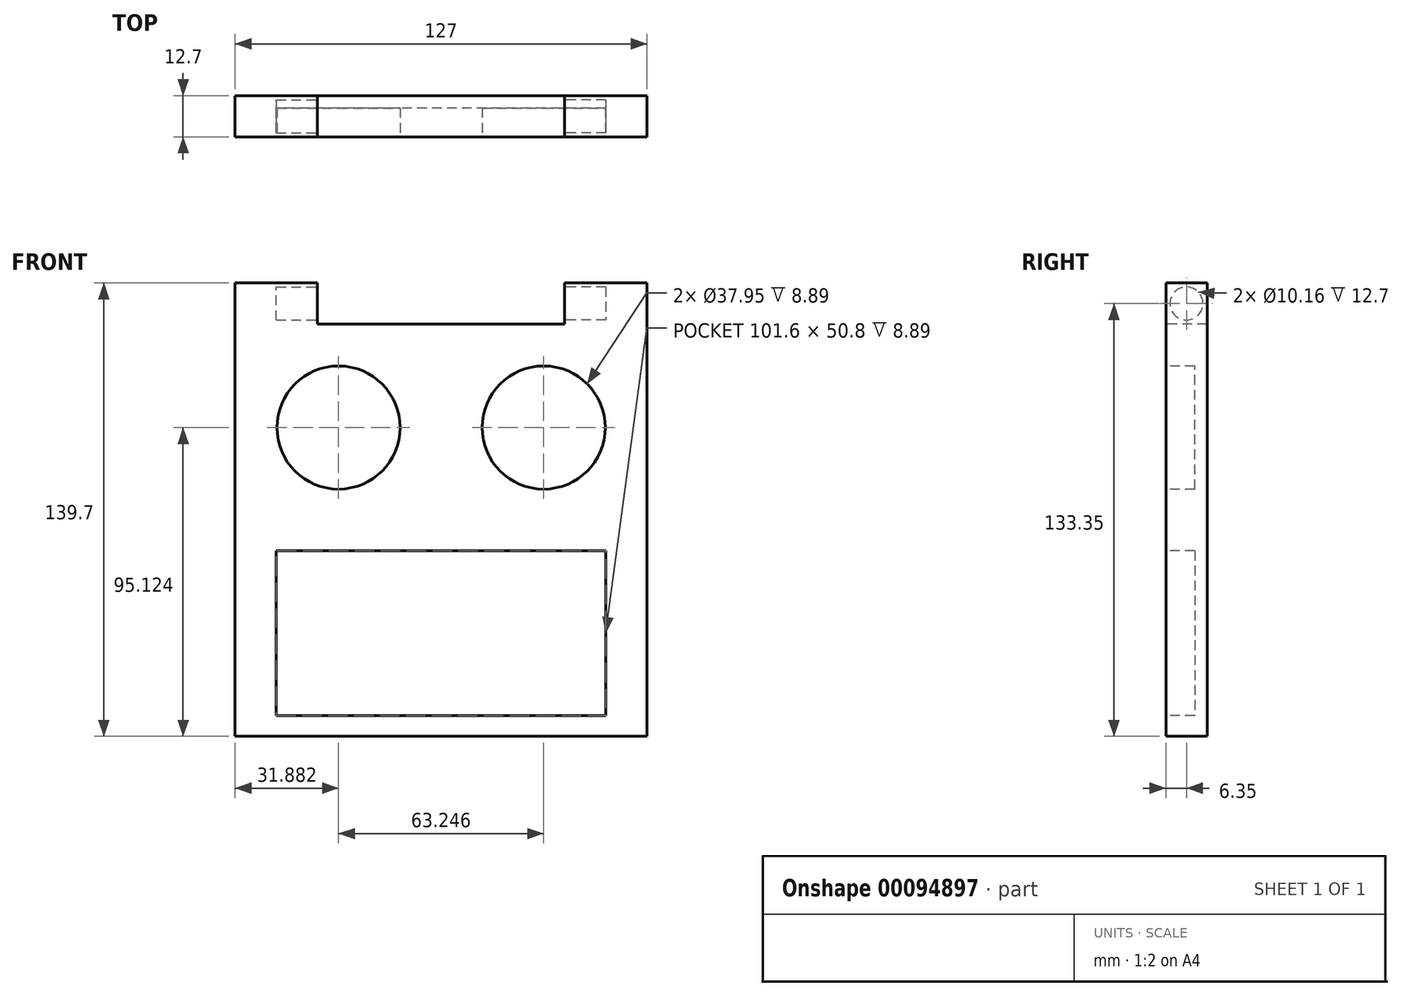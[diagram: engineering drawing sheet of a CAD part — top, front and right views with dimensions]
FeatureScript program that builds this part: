
annotation { "Feature Type Name" : "Feature", "Feature Type Description" : "" }
export const myFeature = defineFeature(function(context is Context, id is Id, definition is map)
    precondition{}
    {
        {
            var Q0;
            Q0=qCreatedBy(makeId("Front.planeOp"),FACE);
            var sketch = newSketch(context, id + "F0", { "sketchPlane" : qUnion([Q0])});
            skLineSegment(sketch, "E0", {"start": v(0, 0) * mm, "end": v(0, 127) * mm});
            skLineSegment(sketch, "E1", {"start": v(0, 127) * mm, "end": v(127, 127) * mm});
            skLineSegment(sketch, "E2", {"start": v(127, 127) * mm, "end": v(127, 0) * mm});
            skLineSegment(sketch, "E3", {"start": v(127, 0) * mm, "end": v(0, 0) * mm});
            skSolve(sketch);
        }
        {
            var Q0;
            Q0=qSketchRegion(id+"F0",true);
            extrude(context, id + "F1", {"entities" : qUnion([Q0]), "depth" : 12.7 * mm});
        }
        {
            var Q0;
            Q0=makeQuery(id+"F1.opExtrude","CAP_FACE",FACE,{"disambiguationData":[OSD([sQuery(id+"F0.wireOp",EDGE,"E0"),sQuery(id+"F0.wireOp",EDGE,"E1"),sQuery(id+"F0.wireOp",EDGE,"E2"),sQuery(id+"F0.wireOp",EDGE,"E3")])],"isStart":false});
            var sketch = newSketch(context, id + "F2", { "sketchPlane" : qUnion([Q0])});
            skCircle(sketch, "E4", {"center": v(95.13, 95.12) * mm, "radius": 18.97 * mm});
            skCircle(sketch, "E5", {"center": v(31.88, 95.12) * mm, "radius": 18.97 * mm});
            skLineSegment(sketch, "E6", {"start": v(12.7, 57.15) * mm, "end": v(12.7, 6.35) * mm});
            skLineSegment(sketch, "E7", {"start": v(12.7, 6.35) * mm, "end": v(114.3, 6.35) * mm});
            skLineSegment(sketch, "E8", {"start": v(114.3, 6.35) * mm, "end": v(114.3, 57.15) * mm});
            skLineSegment(sketch, "E9", {"start": v(114.3, 57.15) * mm, "end": v(12.7, 57.15) * mm});
            skSolve(sketch);
        }
        {
            var Q0;
            Q0=qSketchRegion(id+"F2",true);
            extrude(context, id + "F3", {"entities" : qUnion([Q0]), "operationType" : NewBodyOperationType.REMOVE, "oppositeDirection" : true, "depth" : 8.9 * mm});
        }
        {
            var Q0;
            Q0=makeQuery(id+"F1.opExtrude","SWEPT_FACE",FACE,{"disambiguationData":[OSD([sQuery(id+"F0.wireOp",EDGE,"E1")])]});
            var sketch = newSketch(context, id + "F4", { "sketchPlane" : qUnion([Q0])});
            skLineSegment(sketch, "E10", {"start": v(0, 0) * mm, "end": v(25.4, 0) * mm});
            skLineSegment(sketch, "E11", {"start": v(25.4, 0) * mm, "end": v(25.4, -12.7) * mm});
            skLineSegment(sketch, "E12", {"start": v(25.4, -12.7) * mm, "end": v(0, -12.7) * mm});
            skLineSegment(sketch, "E13", {"start": v(0, -12.7) * mm, "end": v(0, 0) * mm});
            skSolve(sketch);
        }
        {
            var Q0;
            Q0 = qSketchRegion(id + "F4", true);
            extrude(context, id + "F5", {"entities" : qUnion([Q0]), "operationType" : NewBodyOperationType.ADD, "depth" : 12.7 * mm});
        }
        {
            var Q0;
            Q0=makeQuery(id+"F5.opExtrude","SWEPT_FACE",FACE,{"disambiguationData":[OSD([sQuery(id+"F4.wireOp",EDGE,"E11")])]});
            var sketch = newSketch(context, id + "F6", { "sketchPlane" : qUnion([Q0])});
            skCircle(sketch, "E14", {"center": v(-6.35, 133.35) * mm, "radius": 5.08 * mm});
            skPoint(sketch, "E15.trimOffspring.end.orphan", {"position": v(-6.35, 127) * mm});
            skPoint(sketch, "E16.start.orphan", {"position": v(-6.35, 139.7) * mm});
            skSolve(sketch);
        }
        {
            var Q0;
            Q0=makeQuery(id+"F1.opExtrude","SWEPT_FACE",FACE,{"disambiguationData":[OSD([sQuery(id+"F0.wireOp",EDGE,"E1")])]});
            var sketch = newSketch(context, id + "F7", { "sketchPlane" : qUnion([Q0])});
            skLineSegment(sketch, "E17", {"start": v(127, 0) * mm, "end": v(101.6, 0) * mm});
            skLineSegment(sketch, "E18", {"start": v(101.6, 0) * mm, "end": v(101.6, -12.7) * mm});
            skLineSegment(sketch, "E19", {"start": v(101.6, -12.7) * mm, "end": v(127, -12.7) * mm});
            skLineSegment(sketch, "E20", {"start": v(127, -12.7) * mm, "end": v(127, 0) * mm});
            skSolve(sketch);
        }
        {
            var Q0;
            Q0 = qSketchRegion(id + "F7", true);
            extrude(context, id + "F8", {"entities" : qUnion([Q0]), "operationType" : NewBodyOperationType.ADD, "depth" : 12.7 * mm});
        }
        {
            var Q0;
            Q0=makeQuery(id+"F8.opExtrude","SWEPT_FACE",FACE,{"disambiguationData":[OSD([sQuery(id+"F7.wireOp",EDGE,"E18")])]});
            var sketch = newSketch(context, id + "F9", { "sketchPlane" : qUnion([Q0])});
            skCircle(sketch, "E21", {"center": v(6.35, 133.35) * mm, "radius": 5.08 * mm});
            skPoint(sketch, "E22.start.orphan", {"position": v(6.35, 139.7) * mm});
            skPoint(sketch, "E23.trimOffspring.end.orphan", {"position": v(6.35, 127) * mm});
            skSolve(sketch);
        }
        {
            var Q0;
            Q0 = qSketchRegion(id + "F9", true);
            extrude(context, id + "F10", {"entities" : qUnion([Q0]), "operationType" : NewBodyOperationType.REMOVE, "oppositeDirection" : true, "depth" : 12.7 * mm});
        }
        {
            var Q0;
            Q0 = qSketchRegion(id + "F6", true);
            extrude(context, id + "F11", {"entities" : qUnion([Q0]), "operationType" : NewBodyOperationType.REMOVE, "oppositeDirection" : true, "depth" : 12.7 * mm});
        }
    });
